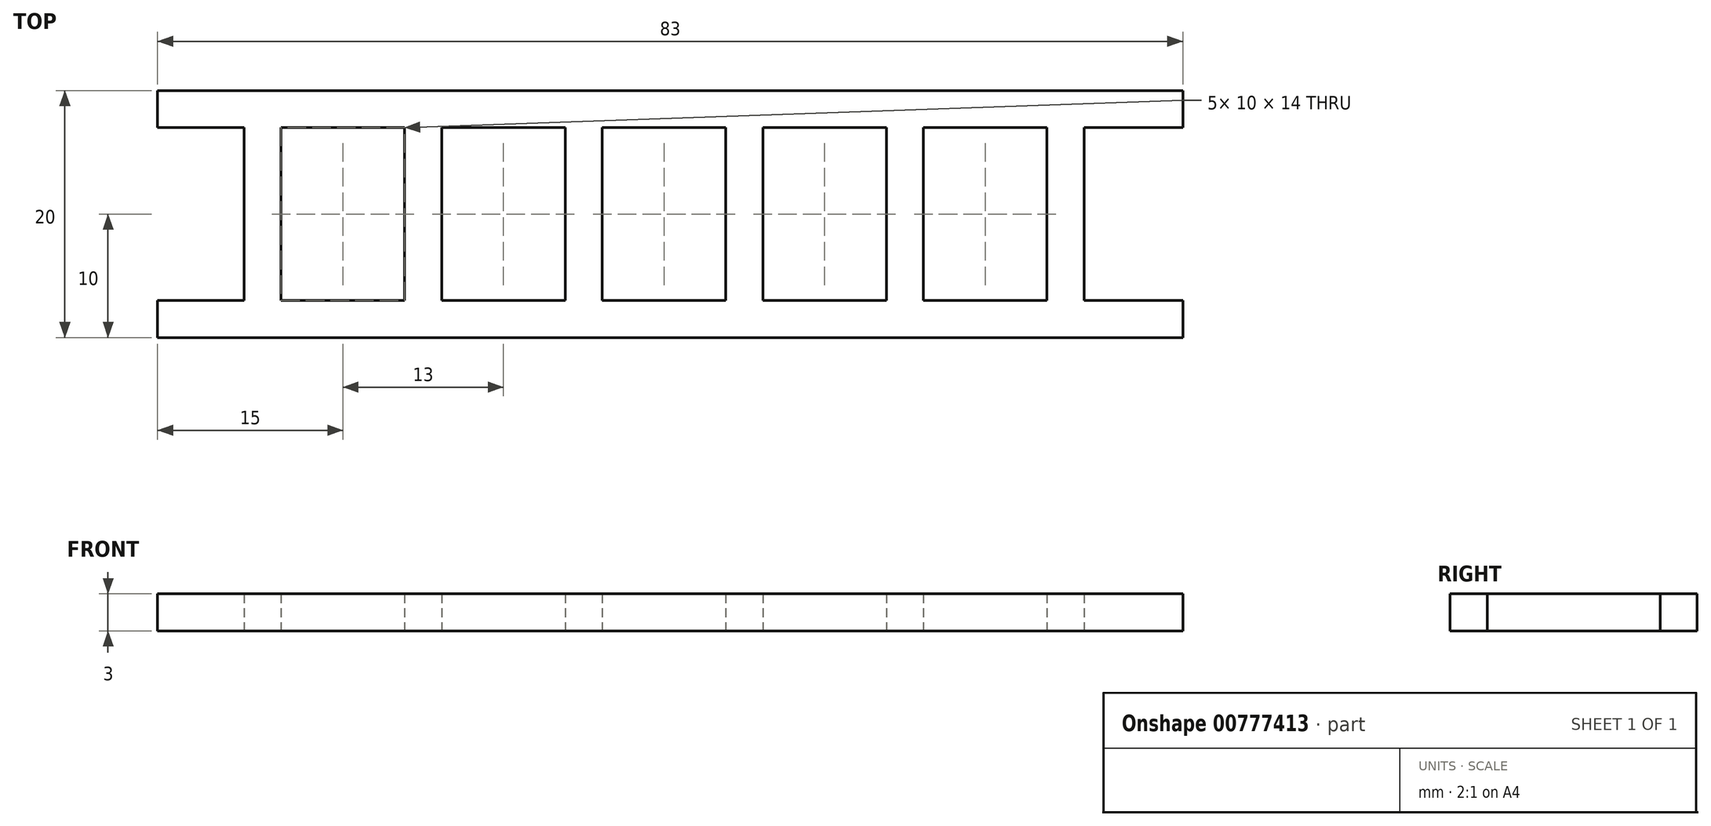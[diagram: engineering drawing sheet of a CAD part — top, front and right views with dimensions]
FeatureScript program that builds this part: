
annotation { "Feature Type Name" : "Feature", "Feature Type Description" : "" }
export const myFeature = defineFeature(function(context is Context, id is Id, definition is map)
    precondition{}
    {
        {
            var Q0;
            Q0=qCreatedBy(makeId("Top.planeOp"),FACE);
            var sketch = newSketch(context, id + "F0", { "sketchPlane" : qUnion([Q0])});
            skLineSegment(sketch, "E0.bottom", {"start": v(0, 0) * mm, "end": v(80, 0) * mm});
            skLineSegment(sketch, "E0.top", {"start": v(0, 20) * mm, "end": v(80, 20) * mm});
            skLineSegment(sketch, "E0.right", {"start": v(80, 0) * mm, "end": v(80, 3) * mm});
            skLineSegment(sketch, "E1.bottom", {"start": v(7, 17) * mm, "end": v(17, 17) * mm});
            skLineSegment(sketch, "E1.top", {"start": v(7, 3) * mm, "end": v(17, 3) * mm});
            skLineSegment(sketch, "E1.left", {"start": v(7, 17) * mm, "end": v(7, 3) * mm});
            skLineSegment(sketch, "E1.right", {"start": v(17, 17) * mm, "end": v(17, 3) * mm});
            skLineSegment(sketch, "E2.1.0.0", {"start": v(30, 17) * mm, "end": v(30, 3) * mm});
            skLineSegment(sketch, "E2.1.0.1", {"start": v(20, 17) * mm, "end": v(30, 17) * mm});
            skLineSegment(sketch, "E2.1.0.2", {"start": v(20, 17) * mm, "end": v(20, 3) * mm});
            skLineSegment(sketch, "E2.1.0.3", {"start": v(20, 3) * mm, "end": v(30, 3) * mm});
            skLineSegment(sketch, "E2.2.0.0", {"start": v(43, 17) * mm, "end": v(43, 3) * mm});
            skLineSegment(sketch, "E2.2.0.1", {"start": v(33, 17) * mm, "end": v(43, 17) * mm});
            skLineSegment(sketch, "E2.2.0.2", {"start": v(33, 17) * mm, "end": v(33, 3) * mm});
            skLineSegment(sketch, "E2.2.0.3", {"start": v(33, 3) * mm, "end": v(43, 3) * mm});
            skLineSegment(sketch, "E2.3.0.0", {"start": v(56, 17) * mm, "end": v(56, 3) * mm});
            skLineSegment(sketch, "E2.3.0.1", {"start": v(46, 17) * mm, "end": v(56, 17) * mm});
            skLineSegment(sketch, "E2.3.0.2", {"start": v(46, 17) * mm, "end": v(46, 3) * mm});
            skLineSegment(sketch, "E2.3.0.3", {"start": v(46, 3) * mm, "end": v(56, 3) * mm});
            skLineSegment(sketch, "E2.4.0.0", {"start": v(69, 17) * mm, "end": v(69, 3) * mm});
            skLineSegment(sketch, "E2.4.0.1", {"start": v(59, 17) * mm, "end": v(69, 17) * mm});
            skLineSegment(sketch, "E2.4.0.2", {"start": v(59, 17) * mm, "end": v(59, 3) * mm});
            skLineSegment(sketch, "E2.4.0.3", {"start": v(59, 3) * mm, "end": v(69, 3) * mm});
            skLineSegment(sketch, "E2.direction1", {"start": v(17, 3) * mm, "end": v(30, 3) * mm, "construction": true});
            skLineSegment(sketch, "E3.0", {"start": v(4, 17) * mm, "end": v(4, 3) * mm});
            skLineSegment(sketch, "E4", {"start": v(4, 17) * mm, "end": v(0, 17) * mm});
            skLineSegment(sketch, "E5", {"start": v(4, 3) * mm, "end": v(0, 3) * mm});
            skLineSegment(sketch, "E6.0", {"start": v(72, 17) * mm, "end": v(72, 3) * mm});
            skLineSegment(sketch, "E7", {"start": v(72, 17) * mm, "end": v(80, 17) * mm});
            skLineSegment(sketch, "E8", {"start": v(72, 3) * mm, "end": v(80, 3) * mm});
            skLineSegment(sketch, "E9", {"start": v(0, 3) * mm, "end": v(-3, 3) * mm});
            skLineSegment(sketch, "E10", {"start": v(0, 17) * mm, "end": v(-3, 17) * mm});
            skLineSegment(sketch, "E11", {"start": v(-3, 17) * mm, "end": v(-3, 20) * mm});
            skLineSegment(sketch, "E12", {"start": v(-3, 20) * mm, "end": v(0, 20) * mm});
            skLineSegment(sketch, "E13", {"start": v(-3, 3) * mm, "end": v(-3, 0) * mm});
            skLineSegment(sketch, "E14", {"start": v(-3, 0) * mm, "end": v(0, 0) * mm});
            skLineSegment(sketch, "E15.trimOffspring", {"start": v(80, 17) * mm, "end": v(80, 20) * mm});
            skSolve(sketch);
        }
        {
            var Q0;
            Q0=makeQuery(id+"F0.imprint","IMPRINT",FACE,{"disambiguationData":[TD([[makeQuery(id+"F0.imprint","IMPRINT",EDGE,{"derivedFrom":sQuery(id+"F0.wireOp",EDGE,"E0.bottom")}),1.0]])]});
            extrude(context, id + "F1", {"entities" : qUnion([Q0]), "depth" : 3 * mm, "offsetDistance" : 25 * mm});
        }
    });
